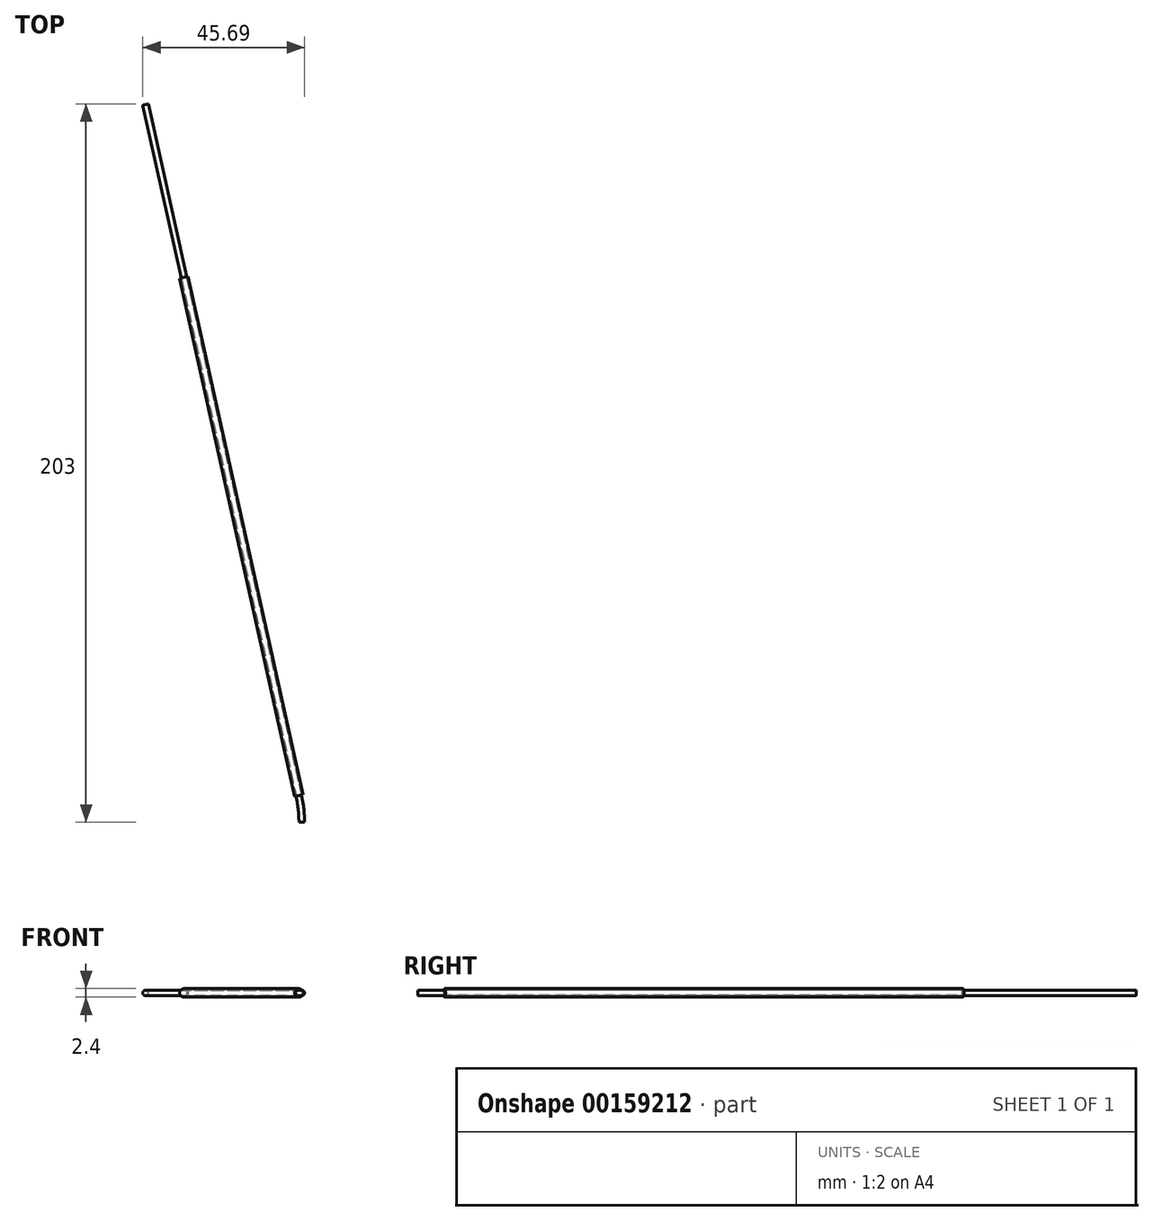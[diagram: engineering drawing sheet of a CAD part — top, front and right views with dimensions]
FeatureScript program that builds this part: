
annotation { "Feature Type Name" : "Feature", "Feature Type Description" : "" }
export const myFeature = defineFeature(function(context is Context, id is Id, definition is map)
    precondition{}
    {
        {
            assignVariable(context, id + "F0", {"name" : "TubeTransmissionLength", "anyValue" : 200});
        }
        {
            assignVariable(context, id + "F1", {"name" : "Angle", "anyValue" : 12.5});
        }
        {
            var Q0;
            Q0=qCreatedBy(makeId("Front.planeOp"),FACE);
            var sketch = newSketch(context, id + "F2", { "sketchPlane" : qUnion([Q0])});
            skCircle(sketch, "E0", {"center": v(0, 0) * mm, "radius": 0.7 * mm});
            skCircle(sketch, "E1", {"center": v(0, 0) * mm, "radius": 0.8 * mm});
            skSolve(sketch);
        }
        {
            var Q0;
            Q0=qCreatedBy(makeId("Top.planeOp"),FACE);
            var sketch = newSketch(context, id + "F3", { "sketchPlane" : qUnion([Q0])});
            skLineSegment(sketch, "E2", {"start": v(0, 0) * mm, "end": v(0, -200) * mm});
            skLineSegment(sketch, "E3", {"start": v(0, -145.32) * mm, "end": v(0, -200) * mm, "construction": true});
            skLineSegment(sketch, "E4", {"start": v(0, -200) * mm, "end": v(-35, -200) * mm, "construction": true});
            skArc(sketch, "E5", {"start": v(0, -200) * mm, "mid": v(-0.2, -203.8) * mm, "end": v(-0.83, -207.57) * mm});
            skSolve(sketch);
        }
        {
            var Q0;
            Q0=makeQuery(id+"F2.imprint","IMPRINT",FACE,{"disambiguationData":[TD([[makeQuery(id+"F2.imprint","IMPRINT",EDGE,{"derivedFrom":sQuery(id+"F2.wireOp",EDGE,"E0")}),-1.0]])]});
            var Q1;
            Q1=sQuery(id+"F3.wireOp",EDGE,"E2");
            var Q2;
            Q2=sQuery(id+"F3.wireOp",EDGE,"E5");
            sweep(context, id + "F4", {"profiles" : qUnion([Q0]), "path" : qUnion([Q1, Q2])});
        }
        {
            var Q0;
            Q0=makeQuery(id+"F4.opSweep","CAP_FACE",FACE,{"disambiguationData":[OSD([sQuery(id+"F2.wireOp",EDGE,"E0"),sQuery(id+"F2.wireOp",EDGE,"E1"),sQuery(id+"F3.wireOp",VERTEX,"E2.start")])],"isStart":true});
            cPlane(context, id + "F5", {"entities" : qUnion([Q0]), "cplaneType" : CPlaneType.OFFSET, "offset" : 50 * mm, "oppositeDirection" : true, "width" : 150 * mm, "height" : 150 * mm});
        }
        {
            var Q0;
            Q0=qCreatedBy(id+"F5.planeOp",FACE);
            var sketch = newSketch(context, id + "F6", { "sketchPlane" : qUnion([Q0])});
            skCircle(sketch, "E6.0", {"center": v(0, 0) * mm, "radius": 0.8 * mm});
            skCircle(sketch, "E6.1", {"center": v(0, 0) * mm, "radius": 0.7 * mm});
            skCircle(sketch, "E7", {"center": v(0, 0) * mm, "radius": 0.9 * mm});
            skCircle(sketch, "E8", {"center": v(0, 0) * mm, "radius": 1.2 * mm});
            skSolve(sketch);
        }
        {
            var Q0;
            Q0=makeQuery(id+"F6.imprint","IMPRINT",FACE,{"disambiguationData":[TD([[makeQuery(id+"F6.imprint","IMPRINT",EDGE,{"derivedFrom":sQuery(id+"F6.wireOp",EDGE,"E7")}),-1.0]])]});
            var Q1;
            Q1=makeQuery(id+"F4.opSweep","SWEPT_FACE",FACE,{"disambiguationData":[OSD([sQuery(id+"F2.wireOp",EDGE,"E1"),sQuery(id+"F3.wireOp",EDGE,"E2")])]});
            extrude(context, id + "F7", {"entities" : qUnion([Q0]), "oppositeDirection" : true, "endBoundEntityFace" : qUnion([Q1]), "depth" : (getVariable(context, 'TubeTransmissionLength') - 50) * mm});
        }
        {
            var Q0;
            Q0=makeQuery(id+"F7.opExtrude","CAP_FACE",FACE,{"disambiguationData":[OSD([sQuery(id+"F6.wireOp",EDGE,"E7"),sQuery(id+"F6.wireOp",EDGE,"E8")])],"isStart":true});
            cPlane(context, id + "F8", {"entities" : qUnion([Q0]), "cplaneType" : CPlaneType.OFFSET, "offset" : 50 * mm, "oppositeDirection" : true, "width" : 150 * mm, "height" : 150 * mm});
        }
        {
            var Q0;
            Q0=qCreatedBy(id+"F8.planeOp",FACE);
            var sketch = newSketch(context, id + "F9", { "sketchPlane" : qUnion([Q0])});
            skCircle(sketch, "E9.0", {"center": v(0, 0) * mm, "radius": 1.2 * mm});
            skLineSegment(sketch, "E10", {"start": v(0, 0) * mm, "end": v(0, 9.07) * mm});
            skLineSegment(sketch, "E11", {"start": v(0, 0) * mm, "end": v(-8.67, 0) * mm});
            skSolve(sketch);
        }
        {
            var Q0;
            Q0=makeQuery(id+"F7.opExtrude","SWEPT_BODY",BODY,{"disambiguationData":[OSD([sQuery(id+"F6.wireOp",EDGE,"E7"),sQuery(id+"F6.wireOp",EDGE,"E8")])]});
            var Q1;
            Q1=makeQuery(id+"F4.opSweep","SWEPT_BODY",BODY,{"disambiguationData":[OSD([sQuery(id+"F2.wireOp",EDGE,"E0"),sQuery(id+"F2.wireOp",EDGE,"E1"),sQuery(id+"F3.wireOp",EDGE,"E5")])]});
            transform(context, id + "F10", {"entities" : qUnion([Q0, Q1]), "transformType" : TransformType.TRANSLATION_3D, "dx" : 0 * mm, "dy" : 4.7 * mm, "dz" : 0 * mm, "makeCopy" : false});
        }
        {
            var Q0;
            Q0=makeQuery(id+"F7.opExtrude","SWEPT_BODY",BODY,{"disambiguationData":[OSD([sQuery(id+"F6.wireOp",EDGE,"E7"),sQuery(id+"F6.wireOp",EDGE,"E8")])]});
            var Q1;
            Q1=makeQuery(id+"F4.opSweep","SWEPT_BODY",BODY,{"disambiguationData":[OSD([sQuery(id+"F2.wireOp",EDGE,"E0"),sQuery(id+"F2.wireOp",EDGE,"E1"),sQuery(id+"F3.wireOp",EDGE,"E5")])]});
            var Q2;
            Q2=sQuery(id+"F9.wireOp",EDGE,"E10");
            transform(context, id + "F11", {"entities" : qUnion([Q0, Q1]), "transformType" : TransformType.ROTATION, "transformAxis" : qUnion([Q2]), "angle" : (getVariable(context, 'Angle')) * degree, "makeCopy" : false});
        }
    });
